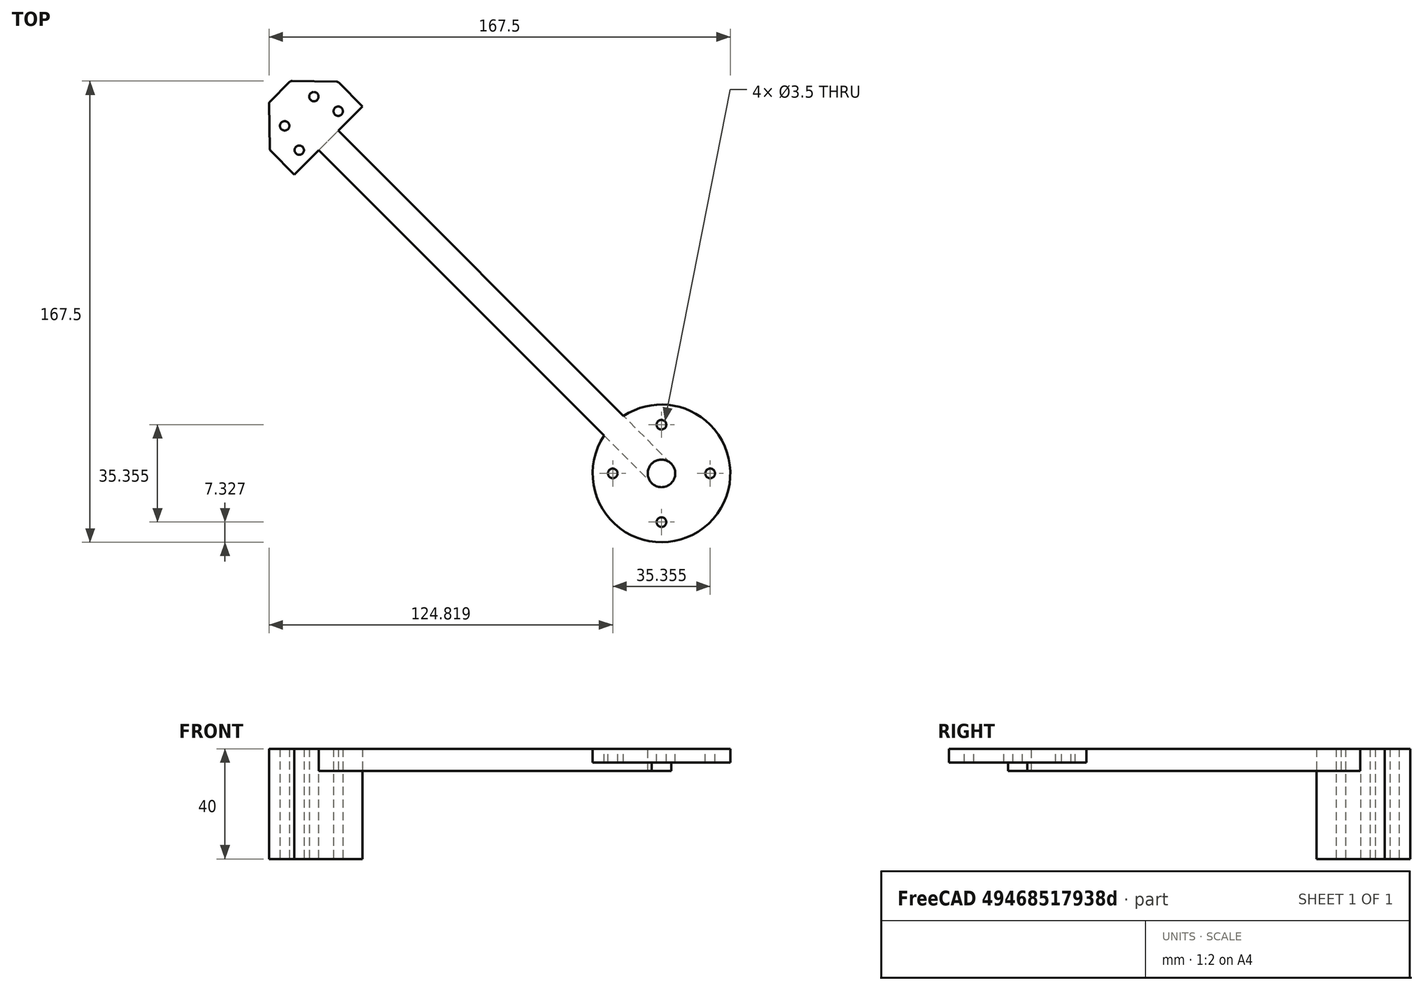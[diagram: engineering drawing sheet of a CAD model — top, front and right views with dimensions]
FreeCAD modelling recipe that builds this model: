
FCSTD DOCUMENT  (FreeCAD 1.0R39285 (Git))
Label: rr-middle-body
License: All rights reserved
LicenseURL: http://en.wikipedia.org/wiki/All_rights_reserved
objects: Sketcher::SketchObject×3, Spreadsheet::Sheet×1, Part::FeaturePython×1, PartDesign::Body×1
note: 8 computed .brp shape members not serialized (recipe doc carries the construction recipe); baked Part::Feature solids carry a one-line shape summary decoded from their .brp

FEATURE [Spreadsheet::Sheet] Spreadsheet
  cells = A1='offset_x; B1(offset_x)=15; A2='offset_y; B2(offset_y)=15; A3='base_x; B3(base_x)=170; A4='base_y; B4(base_y)=180; A5='base_h; B5(base_h)=183.5
FEATURE [Part::FeaturePython] b_leg_001_  label="leg_Body_001"  # a2plus imported part (geometry in sourceFile) (typed FeaturePython)
  Placement = pos=(281.203,-177.571,0) rot=(0,0,1;0.785398rad)
  a2p_Version = 0.4.68
  fixedPosition = true
  objectType = a2pPart
  sourceFile = ./leg.FCStd
  sourcePart = Body
  subassemblyImport = false
  timeLastImport = 1.75319e+09
  updateColors = true
FEATURE [Sketcher::SketchObject] Sketch  label="base_plate"
  ArcFitTolerance = 1e-06
  AttachmentSupport = -> [XY_Plane]
  FullyConstrained = true
  MakeInternals = false
  MapMode = 5
  expr: Constraints[12] = Spreadsheet.offset_y
  expr: Constraints[13] = Spreadsheet.offset_x
  expr: Constraints[18] = Spreadsheet.offset_x
  expr: Constraints[22] = Spreadsheet.base_x
  expr: Constraints[23] = Spreadsheet.base_y
  sketch-geometry (8):
    g0: LineSegment StartX=15 StartY=39.7487 StartZ=0 EndX=39.7487 EndY=15 EndZ=0
    g1: LineSegment StartX=39.7487 StartY=15 StartZ=0 EndX=160.251 EndY=15 EndZ=0
    g2: LineSegment StartX=160.251 StartY=15 StartZ=0 EndX=185 EndY=39.7487 EndZ=0
    g3: LineSegment StartX=185 StartY=39.7487 StartZ=0 EndX=185 EndY=170.251 EndZ=0
    g4: LineSegment StartX=185 StartY=170.251 StartZ=0 EndX=160.251 EndY=195 EndZ=0
    g5: LineSegment StartX=160.251 StartY=195 StartZ=0 EndX=39.7487 EndY=195 EndZ=0
    g6: LineSegment StartX=39.7487 StartY=195 StartZ=0 EndX=15 EndY=170.251 EndZ=0
    g7: LineSegment StartX=15 StartY=170.251 StartZ=0 EndX=15 EndY=39.7487 EndZ=0
  constraints (24):
    c: Coincident(g0,g1)
    c: Horizontal(g1)
    c: Coincident(g1,g2)
    c: Coincident(g2,g3)
    c: Vertical(g3)
    c: Coincident(g3,g4)
    c: Coincident(g4,g5)
    c: Horizontal(g5)
    c: Coincident(g5,g6)
    c: Coincident(g6,g7)
    c: Coincident(g7,g0)
    c: Distance(g0,g0) = 35
    c: DistanceY(g-1,g0) = 15
    c: DistanceX(g-1,g6) = 15
    c: Angle(g1,g0) = 2.35619
    c: Equal(g0,g6)
    c: Equal(g6,g4)
    c: Equal(g4,g2)
    c: DistanceX(g-1,g0) = 15
    c: Horizontal(g2,g0)
    c: Horizontal(g6,g3)
    c: Vertical(g5,g0)
    c: DistanceX(g0,g2) = 170
    c: DistanceY(g0,g5) = 180
FEATURE [Sketcher::SketchObject] Sketch001  label="engine_arm_holes"
  ArcFitTolerance = 1e-06
  AttachmentSupport = -> [XY_Plane]
  FullyConstrained = true
  MakeInternals = false
  MapMode = 5
  expr: Constraints[13] = Spreadsheet.base_x - 47
  expr: Constraints[21] = Spreadsheet.base_h
  expr: Constraints[22] = Spreadsheet.base_h
  expr: Constraints[42] = Spreadsheet.base_h
  expr: Constraints[43] = Spreadsheet.base_h
  expr: Constraints[44] = 10
  sketch-geometry (16):
    g0: Circle CenterX=32.5993 CenterY=42.7041 CenterZ=0 NormalX=0 NormalY=0 NormalZ=1 AngleXU=0 Radius=1.5
    g1: Circle CenterX=43.5 CenterY=32.4 CenterZ=0 NormalX=0 NormalY=0 NormalZ=1 AngleXU=0 Radius=1.5
    g2: Circle CenterX=24 CenterY=37.6 CenterZ=0 NormalX=0 NormalY=0 NormalZ=1 AngleXU=0 Radius=1.5
    g3: Circle CenterX=38.1841 CenterY=23.5 CenterZ=0 NormalX=0 NormalY=0 NormalZ=1 AngleXU=0 Radius=1.5
    g4: Circle CenterX=161.184 CenterY=23.5 CenterZ=0 NormalX=0 NormalY=0 NormalZ=1 AngleXU=0 Radius=1.5
    g5: Circle CenterX=176.085 CenterY=36.8406 CenterZ=0 NormalX=0 NormalY=0 NormalZ=1 AngleXU=0 Radius=1.5
    g6: Circle CenterX=167.984 CenterY=42.7041 CenterZ=0 NormalX=0 NormalY=0 NormalZ=1 AngleXU=0 Radius=1.5
    g7: Circle CenterX=168.148 CenterY=167.067 CenterZ=0 NormalX=0 NormalY=0 NormalZ=1 AngleXU=0 Radius=1.5
    g8: Circle CenterX=157.247 CenterY=177.371 CenterZ=0 NormalX=0 NormalY=0 NormalZ=1 AngleXU=0 Radius=1.5
    g9: Circle CenterX=162.301 CenterY=186 CenterZ=0 NormalX=0 NormalY=0 NormalZ=1 AngleXU=0 Radius=1.5
    g10: Circle CenterX=176.748 CenterY=172.17 CenterZ=0 NormalX=0 NormalY=0 NormalZ=1 AngleXU=0 Radius=1.5
    g11: Circle CenterX=32.5993 CenterY=166.896 CenterZ=0 NormalX=0 NormalY=0 NormalZ=1 AngleXU=0 Radius=1.5
    g12: Circle CenterX=43.3361 CenterY=177.371 CenterZ=0 NormalX=0 NormalY=0 NormalZ=1 AngleXU=0 Radius=1.5
    g13: Circle CenterX=38.2829 CenterY=186 CenterZ=0 NormalX=0 NormalY=0 NormalZ=1 AngleXU=0 Radius=1.5
    g14: Circle CenterX=24 CenterY=172 CenterZ=0 NormalX=0 NormalY=0 NormalZ=1 AngleXU=0 Radius=1.5
    g15: Circle CenterX=157.247 CenterY=32.2293 CenterZ=0 NormalX=0 NormalY=0 NormalZ=1 AngleXU=0 Radius=1.5
  constraints (48):
    c: Equal(g1,g0)
    c: Equal(g0,g2)
    c: Equal(g2,g3)
    c: Distance(g3,g2) = 20
    c: Distance(g0,g1) = 15
    c: Radius(g2) = 1.5
    c: Distance(g2,g0) = 10
    c: DistanceY(g-1,g2) = 37.6
    c: DistanceX(g-1,g2) = 24
    c: DistanceY(g-1,g3) = 23.5
    c: DistanceY(g-1,g1) = 32.4
    c: DistanceX(g-1,g1) = 43.5
    c: Horizontal(g4,g3)
    c: DistanceX(g3,g4) = 123
    c: Horizontal(g0,g6)
    c: Distance(g4,g5) = 20
    c: Equal(g10,g8)
    c: Equal(g8,g9)
    c: Distance(g10,g9) = 20
    c: Distance(g7,g8) = 15
    c: Distance(g7,g10) = 10
    c: Distance(g1,g7) = 183.5
    c: Distance(g8,g0) = 183.5
    c: Distance(g8,g9) = 10
    c: Equal(g8,g12)
    c: Equal(g12,g13)
    c: Equal(g13,g11)
    c: Vertical(g2,g14)
    c: Vertical(g0,g11)
    c: Distance(g14,g13) = 20
    c: Distance(g11,g12) = 15
    c: Distance(g14,g11) = 10
    c: Distance(g13,g12) = 10
    c: DistanceY(g-1,g14) = 172
    c: DistanceY(g-1,g13) = 186
    c: Horizontal(g8,g12)
    c: Horizontal(g9,g13)
    c: Equal(g1,g4)
    c: Equal(g4,g15)
    c: Equal(g15,g5)
    c: Equal(g5,g6)
    c: Distance(g15,g6) = 15
    c: Distance(g11,g15) = 183.5
    c: Distance(g6,g12) = 183.5
    c: Distance(g5,g6) = 10
    c: Equal(g10,g7)
    c: Equal(g9,g1)
    c: Equal(g13,g14)
FEATURE [Sketcher::SketchObject] Sketch002  label="mounting_plate"
  ArcFitTolerance = 1e-06
  AttachmentSupport = -> [XY_Plane]
  FullyConstrained = true
  MakeInternals = false
  MapMode = 5
  expr: Constraints[11] = Spreadsheet.base_x - 33 * 2
  expr: Constraints[8] = Spreadsheet.offset_x + 25
  expr: Constraints[9] = Spreadsheet.offset_x + 33
  sketch-geometry (4):
    g0: LineSegment StartX=40 StartY=194.944 StartZ=0 EndX=48 EndY=186 EndZ=0
    g1: LineSegment StartX=48 StartY=186 StartZ=0 EndX=152 EndY=186 EndZ=0
    g2: LineSegment StartX=152 StartY=186 StartZ=0 EndX=160 EndY=194.944 EndZ=0
    g3: LineSegment StartX=160 StartY=194.944 StartZ=0 EndX=40 EndY=194.944 EndZ=0
  constraints (12):
    c: Coincident(g0,g1)
    c: Horizontal(g1)
    c: Coincident(g1,g2)
    c: Coincident(g2,g3)
    c: Coincident(g3,g0)
    c: Horizontal(g3)
    c: Distance(g0,g0) = 12
    c: Equal(g0,g2)
    c: DistanceX(g-1,g0) = 40
    c: DistanceX(g-1,g0) = 48
    c: DistanceY(g-1,g0) = 186
    c: DistanceX(g0,g1) = 104
FEATURE [PartDesign::Body] Body
  AllowCompound = false
  Group = -> [Sketch,Sketch001,Sketch002]
  Origin = -> Origin
